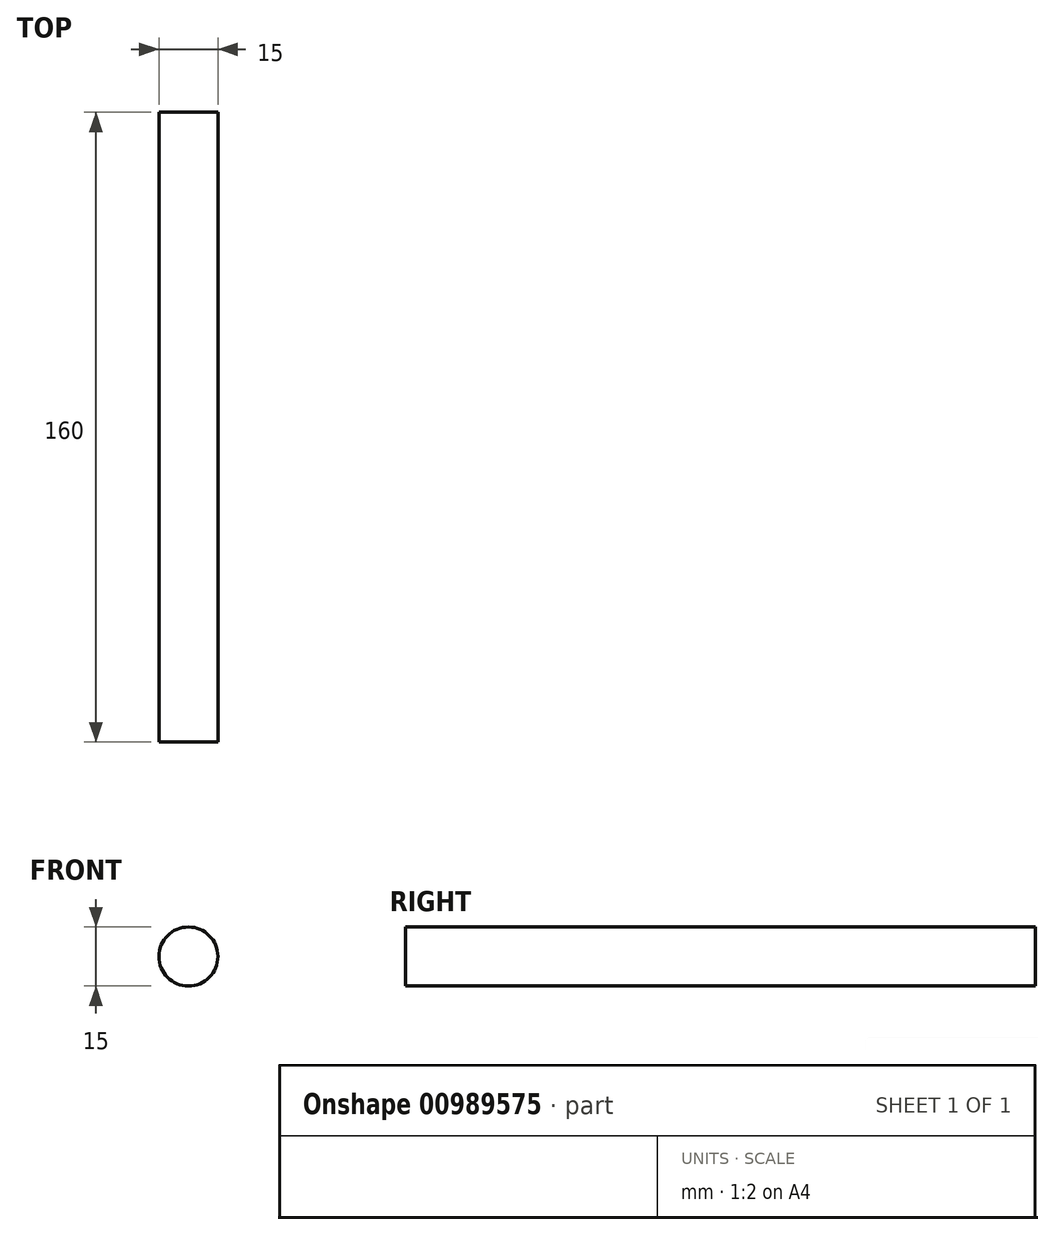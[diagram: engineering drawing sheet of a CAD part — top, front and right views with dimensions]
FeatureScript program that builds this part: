
annotation { "Feature Type Name" : "Feature", "Feature Type Description" : "" }
export const myFeature = defineFeature(function(context is Context, id is Id, definition is map)
    precondition{}
    {
        {
            var Q0;
            Q0=qCreatedBy(makeId("Front.planeOp"), FACE);
            var sketch = newSketch(context, id + "F0", { "sketchPlane" : qUnion([Q0])});
            skCircle(sketch, "E0", {"center": v(0, 0) * mm, "radius": 7.5 * mm});
            skSolve(sketch);
        }
        {
            var Q0;
            Q0 = qSketchRegion(id + "F0", true);
            extrude(context, id + "F1", {"entities" : qUnion([Q0]), "domain" : OperationDomain.MODEL, "flatOperationType" : FlatOperationType.REMOVE, "depth" : 160 * mm, "offsetDistance" : 25 * mm});
        }
    });
